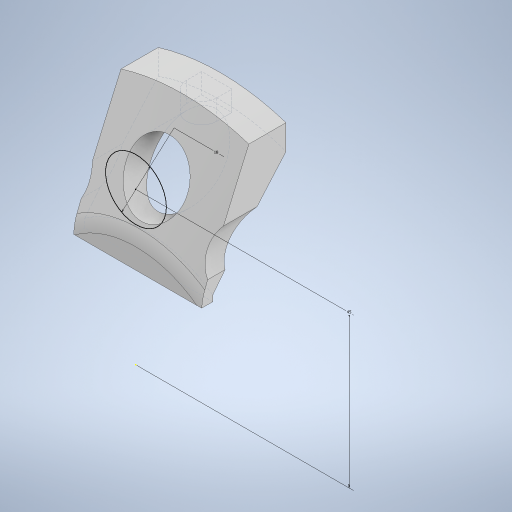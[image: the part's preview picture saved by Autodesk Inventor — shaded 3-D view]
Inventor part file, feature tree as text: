
AUTODESK INVENTOR PART (.ipt)
format: ipt  version: 2023 (Build 270158000, 158)  size: 369,152 bytes
history: native  units: mm
features: sketch x5, extrude x4, revolve x1, fillet x1, plane x1, pattern_circular x1
ambient origin geometry x8: Origin, YZ Plane, XZ Plane, XY Plane, X Axis, Y Axis, Z Axis, Center Point
bodies: Solid1 (feature_tree)
feature tree (13):
  extrude  "Extrusion1"  Depth=19.0mm
  revolve  "Revolution1"  [1 undecoded]
  fillet  "Fillet1"  Radius=7.0mm
  plane  "Work Plane2"
  extrude  "Extrusion2"  Depth=11.0mm
  sketch  "Sketch4"  dims[d11=30.0mm d12=90.0deg]
  extrude  "Extrusion3"  TaperAngle=90.0deg  [1 undecoded]
  pattern_circular  "Circular Pattern1"  [2 undecoded]
  extrude  "Extrusion4"  Depth=9.0mm TaperAngle=0.0deg
  sketch  "Sketch1"  dims[d0=22.0mm d1=19.0mm]
  sketch  "Sketch2"  dims[d2=65.0mm d3=3.3mm d4=0.0mm d8=7.0mm]
  sketch  "Sketch3"  dims[d9=25.0mm d10=11.0mm]
  sketch  "Sketch5"  dims[d13=10.0mm d14=9.0mm d19=61.0mm d20=6.0mm d21=0.0mm d22=1.0mm d23=0.0mm d24=0.0mm d25=45.0mm d26=18.0mm d27=100.0mm d28=360.0deg d30=0.0mm d31=0.0mm]
note: 4 required parameter values undecoded (feature->parameter linkage not recoverable at this tier; creation-order binding heuristic only, values carry confidence <= 0.55)